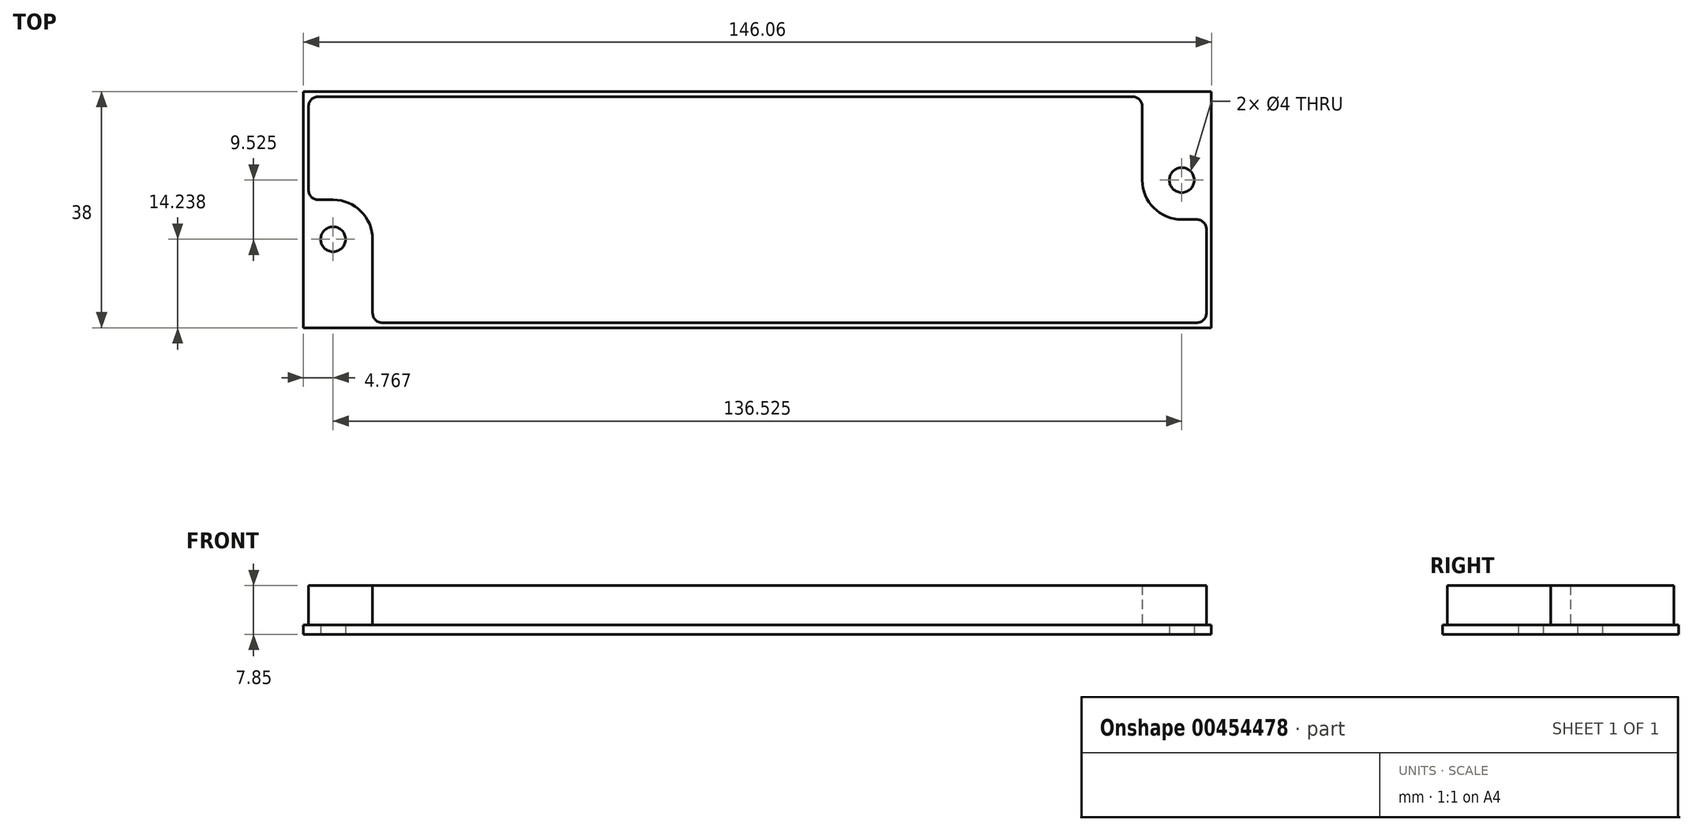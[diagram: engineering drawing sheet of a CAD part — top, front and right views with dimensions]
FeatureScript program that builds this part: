
annotation { "Feature Type Name" : "Feature", "Feature Type Description" : "" }
export const myFeature = defineFeature(function(context is Context, id is Id, definition is map)
    precondition{}
    {
        {
            var Q0;
            Q0=qCreatedBy(makeId("Top.planeOp"),FACE);
            var sketch = newSketch(context, id + "F0", { "sketchPlane" : qUnion([Q0])});
            skLineSegment(sketch, "E0.bottom", {"start": v(-73.03, 19) * mm, "end": v(73.03, 19) * mm, "construction": true});
            skLineSegment(sketch, "E0.top", {"start": v(-73.03, -19) * mm, "end": v(73.03, -19) * mm, "construction": true});
            skLineSegment(sketch, "E0.left", {"start": v(-73.03, 19) * mm, "end": v(-73.03, -19) * mm, "construction": true});
            skLineSegment(sketch, "E0.right", {"start": v(73.03, 19) * mm, "end": v(73.03, -19) * mm, "construction": true});
            skCircle(sketch, "E1", {"center": v(-68.26, -4.76) * mm, "radius": 4.76 * mm});
            skPoint(sketch, "E2.third.point.positionSnap0", {"position": v(73.03, 0) * mm});
            skCircle(sketch, "E3", {"center": v(68.26, 4.76) * mm, "radius": 4.76 * mm});
            skPoint(sketch, "E4", {"position": v(0, 19) * mm});
            skLineSegment(sketch, "E5.bottom", {"start": v(-73.03, 19) * mm, "end": v(73.03, 19) * mm});
            skLineSegment(sketch, "E5.top", {"start": v(-73.03, -19) * mm, "end": v(73.03, -19) * mm});
            skLineSegment(sketch, "E5.left", {"start": v(-73.03, 19) * mm, "end": v(-73.03, -19) * mm});
            skLineSegment(sketch, "E5.right", {"start": v(73.03, 19) * mm, "end": v(73.03, -19) * mm});
            skCircle(sketch, "E6", {"center": v(-68.26, -4.76) * mm, "radius": 2 * mm});
            skCircle(sketch, "E7", {"center": v(68.26, 4.76) * mm, "radius": 2 * mm});
            skArc(sketch, "E8", {"start": v(68.26, 11.11) * mm, "mid": v(61.91, 4.76) * mm, "end": v(68.26, -1.59) * mm});
            skArc(sketch, "E9", {"start": v(-68.26, -11.11) * mm, "mid": v(-61.91, -4.76) * mm, "end": v(-68.26, 1.59) * mm});
            skLineSegment(sketch, "E10", {"start": v(68.26, 11.11) * mm, "end": v(73.03, 11.11) * mm});
            skLineSegment(sketch, "E11", {"start": v(68.26, -1.59) * mm, "end": v(73.03, -1.59) * mm});
            skLineSegment(sketch, "E12", {"start": v(-68.26, 1.59) * mm, "end": v(-73.03, 1.59) * mm});
            skLineSegment(sketch, "E13", {"start": v(-68.26, -11.11) * mm, "end": v(-73.03, -11.11) * mm});
            skSolve(sketch);
        }
        {
            var Q0;
            {var subQ3=sQuery(id+"F0.wireOp",EDGE,"E5.bottom");Q0=makeQuery(id+"F0.imprint","IMPRINT",FACE,{"disambiguationData":[TD([[makeQuery(id+"F0.imprint","IMPRINT",EDGE,{"derivedFrom":subQ3}),-1.0]])]});}
            var Q1;
            {var subQ2=sQuery(id+"F0.wireOp",EDGE,"98831978-42fd-4fc3-8ba1-c0d78f31e865");Q1=makeQuery(id+"F0.imprint","IMPRINT",FACE,{"disambiguationData":[TD([[makeQuery(id+"F0.imprint","IMPRINT",EDGE,{"derivedFrom":subQ2}),-1.0]])]});}
            var Q2;
            Q2=makeQuery(id+"F0.imprint","IMPRINT",FACE,{"disambiguationData":[TD([[makeQuery(id+"F0.imprint","IMPRINT",EDGE,{"derivedFrom":sQuery(id+"F0.wireOp",EDGE,"98831978-42fd-4fc3-8ba1-c0d78f31e865")}),1.0]])]});
            var Q3;
            {var subQ2=sQuery(id+"F0.wireOp",EDGE,"E1");Q3=makeQuery(id+"F0.imprint","IMPRINT",FACE,{"disambiguationData":[TD([[makeQuery(id+"F0.imprint","IMPRINT",EDGE,{"derivedFrom":subQ2}),-1.0]])]});}
            var Q4;
            Q4=makeQuery(id+"F0.imprint","IMPRINT",FACE,{"disambiguationData":[TD([[makeQuery(id+"F0.imprint","IMPRINT",EDGE,{"derivedFrom":sQuery(id+"F0.wireOp",EDGE,"E1")}),1.0]])]});
            var Q5;
            {var subQ2=sQuery(id+"F0.wireOp",EDGE,"E3");Q5=makeQuery(id+"F0.imprint","IMPRINT",FACE,{"disambiguationData":[TD([[makeQuery(id+"F0.imprint","IMPRINT",EDGE,{"derivedFrom":subQ2}),-1.0]])]});}
            var Q6;
            Q6=makeQuery(id+"F0.imprint","IMPRINT",FACE,{"disambiguationData":[TD([[makeQuery(id+"F0.imprint","IMPRINT",EDGE,{"derivedFrom":sQuery(id+"F0.wireOp",EDGE,"E3")}),1.0]])]});
            var Q7;
            {var subQ0=sQuery(id+"F0.wireOp",EDGE,"wPtf7Bfa-nAHX-34n6-2WwW-lTUwI7LqH1O8");Q7=makeQuery(id+"F0.imprint","IMPRINT",FACE,{"disambiguationData":[TD([[makeQuery(id+"F0.imprint","IMPRINT",EDGE,{"derivedFrom":subQ0}),-1.0]])]});}
            var Q8;
            Q8=makeQuery(id+"F0.imprint","IMPRINT",FACE,{"disambiguationData":[TD([[makeQuery(id+"F0.imprint","IMPRINT",EDGE,{"derivedFrom":sQuery(id+"F0.wireOp",EDGE,"wPtf7Bfa-nAHX-34n6-2WwW-lTUwI7LqH1O8")}),1.0]])]});
            extrude(context, id + "F1", {"entities" : qUnion([Q0, Q1, Q2, Q3, Q4, Q5, Q6, Q7, Q8]), "depth" : 1.5 * mm});
        }
        {
            var Q0;
            Q0=makeQuery(id+"F1.opExtrude","CAP_FACE",FACE,{"disambiguationData":[OSD([sQuery(id+"F0.wireOp",EDGE,"E5.bottom"),sQuery(id+"F0.wireOp",EDGE,"E5.top"),sQuery(id+"F0.wireOp",EDGE,"E5.left"),sQuery(id+"F0.wireOp",EDGE,"E5.right"),sQuery(id+"F0.wireOp",EDGE,"DCfoqFDe-yPw3-men3-BHSX-7FplruiKaREZ"),sQuery(id+"F0.wireOp",EDGE,"XyajpIfZ-1DC5-Woiw-QVlM-uBImC3lHlZXN"),sQuery(id+"F0.wireOp",EDGE,"E6"),sQuery(id+"F0.wireOp",EDGE,"E7")])],"isStart":false});
            var sketch = newSketch(context, id + "F2", { "sketchPlane" : qUnion([Q0])});
            skLineSegment(sketch, "E14.0", {"start": v(68.26, -1.59) * mm, "end": v(70.64, -1.59) * mm});
            skArc(sketch, "E14.1", {"start": v(68.26, 11.11) * mm, "mid": v(61.91, 4.76) * mm, "end": v(68.26, -1.59) * mm});
            skLineSegment(sketch, "E14.2", {"start": v(68.26, 11.11) * mm, "end": v(72.23, 11.11) * mm});
            skLineSegment(sketch, "E15.0", {"start": v(73.03, 19) * mm, "end": v(73.03, -19) * mm});
            skLineSegment(sketch, "E15.4", {"start": v(-73.03, -19) * mm, "end": v(73.03, -19) * mm});
            skLineSegment(sketch, "E15.5", {"start": v(-73.03, 19) * mm, "end": v(-73.03, -19) * mm});
            skArc(sketch, "E15.7", {"start": v(-61.91, -4.76) * mm, "mid": v(-63.77, -0.27) * mm, "end": v(-68.26, 1.59) * mm});
            skLineSegment(sketch, "E15.8", {"start": v(-68.26, 1.59) * mm, "end": v(-70.64, 1.59) * mm});
            skLineSegment(sketch, "E15.9", {"start": v(-73.03, 19) * mm, "end": v(73.03, 19) * mm});
            skLineSegment(sketch, "E16.0", {"start": v(-70.64, 18.2) * mm, "end": v(60.32, 18.2) * mm});
            skLineSegment(sketch, "E16.2", {"start": v(-60.32, -18.2) * mm, "end": v(70.64, -18.2) * mm});
            skPoint(sketch, "E17", {"position": v(72.23, -1.59) * mm});
            skLineSegment(sketch, "E18.trimOffspring", {"start": v(72.23, -3.18) * mm, "end": v(72.23, -18.2) * mm});
            skPoint(sketch, "E19.orphan", {"position": v(73.03, 11.11) * mm});
            skPoint(sketch, "E20.orphan", {"position": v(73.03, -1.59) * mm});
            skPoint(sketch, "E21.orphan", {"position": v(-73.03, -11.11) * mm});
            skPoint(sketch, "E22.orphan", {"position": v(-73.03, 1.59) * mm});
            skPoint(sketch, "E23.visualSharp", {"position": v(-72.23, 1.59) * mm});
            skPoint(sketch, "E24.visualSharp", {"position": v(72.23, 11.11) * mm});
            skPoint(sketch, "E25.visualSharp", {"position": v(72.23, 18.2) * mm});
            skPoint(sketch, "E26.orphan", {"position": v(-68.26, -11.11) * mm});
            skPoint(sketch, "E27.visualSharp", {"position": v(-72.22, 18.2) * mm});
            skLineSegment(sketch, "E28", {"start": v(61.91, 4.76) * mm, "end": v(61.91, 16.61) * mm});
            skArc(sketch, "E29.filletArc", {"start": v(61.91, 16.61) * mm, "mid": v(61.45, 17.73) * mm, "end": v(60.32, 18.2) * mm});
            skLineSegment(sketch, "E30.0", {"start": v(-72.23, 16.61) * mm, "end": v(-72.23, 3.18) * mm});
            skLineSegment(sketch, "E31", {"start": v(-61.91, -4.76) * mm, "end": v(-61.91, -16.61) * mm});
            skPoint(sketch, "E32.orphan", {"position": v(-60.32, -18.2) * mm});
            skArc(sketch, "E33.filletArc", {"start": v(-72.23, 3.18) * mm, "mid": v(-71.76, 2.05) * mm, "end": v(-70.64, 1.59) * mm});
            skPoint(sketch, "E34.visualSharp", {"position": v(-61.91, -18.2) * mm});
            skArc(sketch, "E34.filletArc", {"start": v(-61.91, -16.61) * mm, "mid": v(-61.45, -17.73) * mm, "end": v(-60.32, -18.2) * mm});
            skLineSegment(sketch, "E35.0", {"start": v(72.23, -3.18) * mm, "end": v(72.23, -16.61) * mm});
            skArc(sketch, "E36.filletArc", {"start": v(72.23, -3.18) * mm, "mid": v(71.76, -2.05) * mm, "end": v(70.64, -1.59) * mm});
            skArc(sketch, "E37.filletArc", {"start": v(70.64, -18.2) * mm, "mid": v(71.76, -17.73) * mm, "end": v(72.23, -16.61) * mm});
            skArc(sketch, "E38.filletArc", {"start": v(-70.64, 18.2) * mm, "mid": v(-71.76, 17.73) * mm, "end": v(-72.23, 16.61) * mm});
            skSolve(sketch);
        }
        {
            var Q0;
            Q0=makeQuery(id+"F2.imprint","IMPRINT",FACE,{"disambiguationData":[TD([[makeQuery(id+"F2.imprint","IMPRINT",EDGE,{"derivedFrom":sQuery(id+"F2.wireOp",EDGE,"E14.0")}),-1.0]])]});
            extrude(context, id + "F3", {"entities" : qUnion([Q0]), "depth" : 6.35 * mm});
        }
    });
